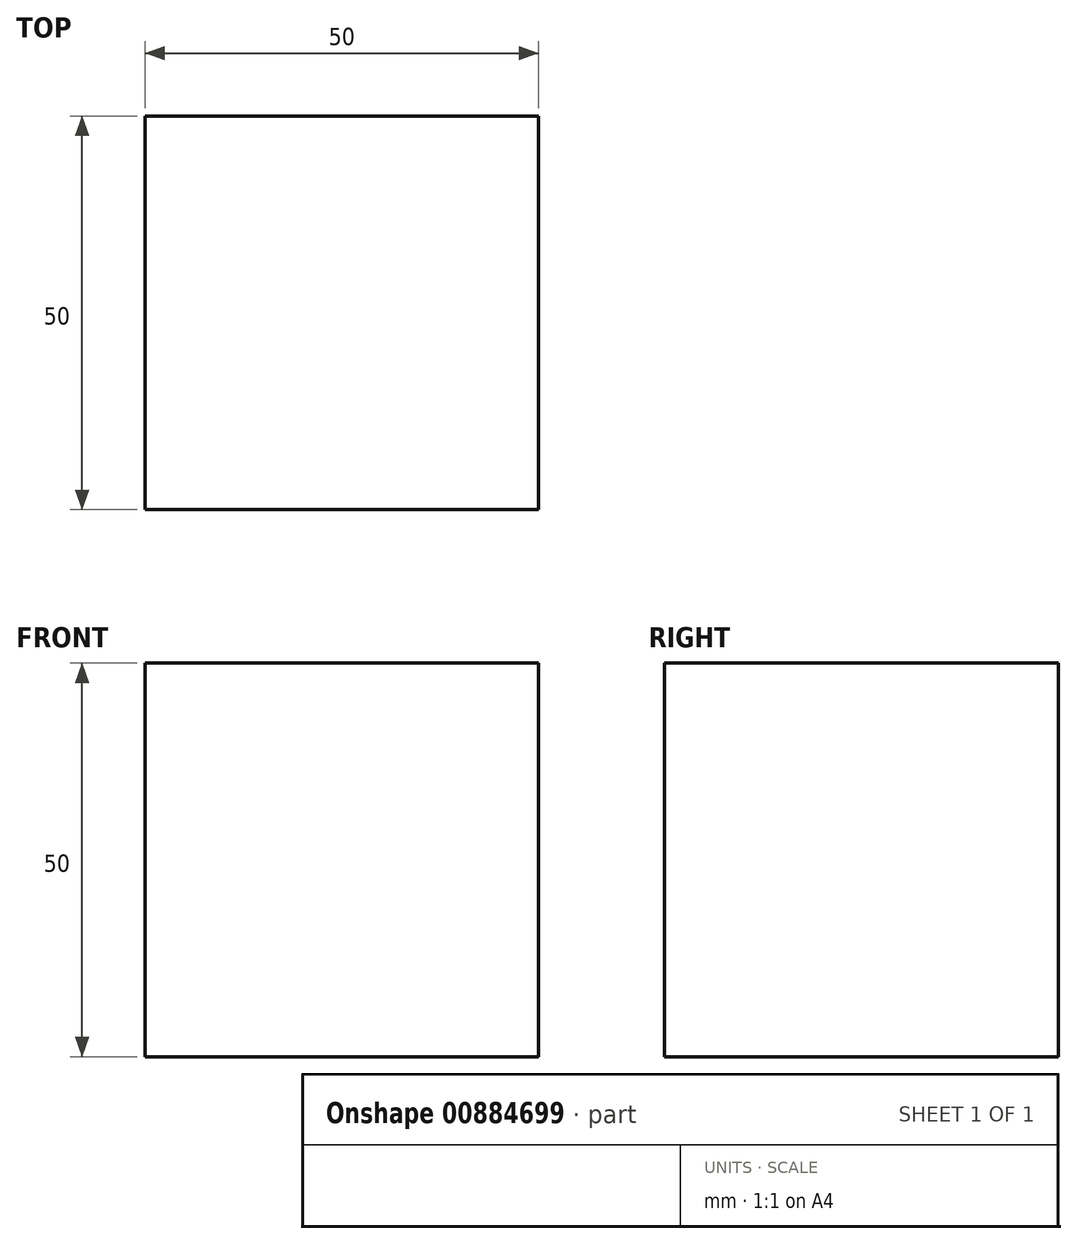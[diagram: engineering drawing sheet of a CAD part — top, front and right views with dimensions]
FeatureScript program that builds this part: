
annotation { "Feature Type Name" : "Feature", "Feature Type Description" : "" }
export const myFeature = defineFeature(function(context is Context, id is Id, definition is map)
    precondition{}
    {
        {
            var Q0;
            Q0=qCreatedBy(makeId("Front.planeOp"),FACE);
            var sketch = newSketch(context, id + "F0", { "sketchPlane" : qUnion([Q0])});
            skLineSegment(sketch, "E0.bottom", {"start": v(0, 0) * mm, "end": v(-50, 0) * mm});
            skLineSegment(sketch, "E0.top", {"start": v(0, 50) * mm, "end": v(-50, 50) * mm});
            skLineSegment(sketch, "E0.left", {"start": v(0, 0) * mm, "end": v(0, 50) * mm});
            skLineSegment(sketch, "E0.right", {"start": v(-50, 0) * mm, "end": v(-50, 50) * mm});
            skSolve(sketch);
        }
        {
            var Q0;
            Q0=makeQuery(id+"F0.imprint","IMPRINT",FACE,{"disambiguationData":[TD([[makeQuery(id+"F0.imprint","IMPRINT",EDGE,{"derivedFrom":sQuery(id+"F0.wireOp",EDGE,"E0.bottom")}),-1.0]])]});
            extrude(context, id + "F1", {"entities" : qUnion([Q0]), "depth" : 50 * mm, "offsetDistance" : 25 * mm});
        }
    });
